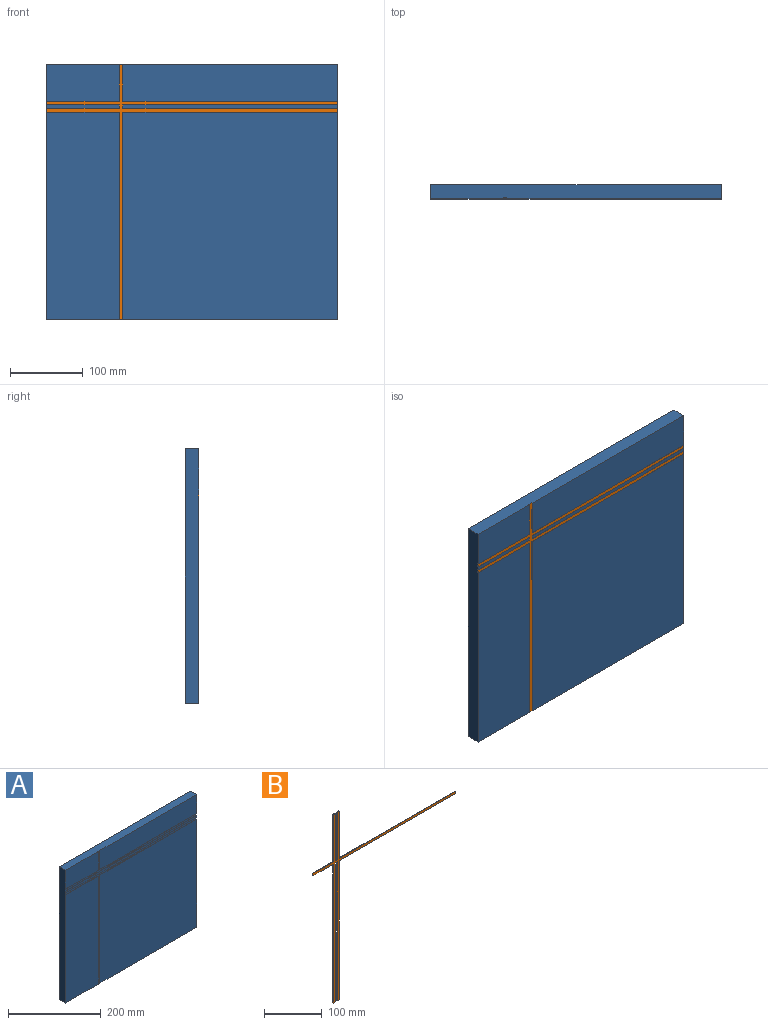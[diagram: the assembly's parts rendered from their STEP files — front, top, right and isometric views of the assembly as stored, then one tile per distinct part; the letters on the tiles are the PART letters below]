
ASSEMBLY  parts=2 mates=1
PART A: 26 faces, bbox 400x19x350 mm
  f0: plane 400x19mm, normal (0,0,1), area 7595mm2, adj f1,f3,f6,f7,f10,f17,f18,f25
  f1: plane 350x19mm, normal (1,0,0), area 6640mm2, adj f0,f2,f3,f4,f8,f10,f12,f13
  f2: plane 295x5mm, normal (0,-1,0), area 1475mm2, adj f1,f13,f14,f15
  f3: plane 295x50mm, normal (0,-1,0), area 14750mm2, adj f0,f1,f16,f17
  f4: plane 295x285mm, normal (0,-1,0), area 84075mm2, adj f1,f8,f11,f12
  f5: plane 100x5mm, normal (0,-1,0), area 500mm2, adj f7,f20,f21,f22
  f6: plane 100x50mm, normal (0,-1,0), area 5000mm2, adj f0,f7,f18,f19
  f7: plane 350x19mm, normal (-1,0,0), area 6640mm2, adj f0,f5,f6,f8,f9,f10,f19,f20
  f8: plane 400x19mm, normal (0,0,-1), area 7595mm2, adj f1,f4,f7,f9,f10,f11,f24,f25
  f9: plane 285x100mm, normal (0,-1,0), area 28500mm2, adj f7,f8,f23,f24
  f10: plane 400x350mm, normal (0,1,0), area 140000mm2, adj f0,f1,f7,f8
  f11: plane 285x1mm, normal (-1,0,0), area 285mm2, adj f4,f8,f12,f25
  f12: plane 295x1mm, normal (0,0,1), area 295mm2, adj f1,f4,f11,f25
  f13: plane 295x1mm, normal (0,0,-1), area 295mm2, adj f1,f2,f14,f25
  f14: plane 5x1mm, normal (-1,0,0), area 5mm2, adj f2,f13,f15,f25
  f15: plane 295x1mm, normal (0,0,1), area 295mm2, adj f1,f2,f14,f25
  f16: plane 295x1mm, normal (0,0,-1), area 295mm2, adj f1,f3,f17,f25
  f17: plane 50x1mm, normal (-1,0,0), area 50mm2, adj f0,f3,f16,f25
  f18: plane 50x1mm, normal (1,0,0), area 50mm2, adj f0,f6,f19,f25
  f19: plane 100x1mm, normal (0,0,-1), area 100mm2, adj f6,f7,f18,f25
  f20: plane 100x1mm, normal (0,0,1), area 100mm2, adj f5,f7,f21,f25
  f21: plane 5x1mm, normal (1,0,0), area 5mm2, adj f5,f20,f22,f25
  f22: plane 100x1mm, normal (0,0,-1), area 100mm2, adj f5,f7,f21,f25
  f23: plane 100x1mm, normal (0,0,1), area 100mm2, adj f7,f9,f24,f25
  f24: plane 285x1mm, normal (1,0,0), area 285mm2, adj f8,f9,f23,f25
  f25: plane 400x350mm, normal (0,-1,0), area 5700mm2, adj f0,f1,f7,f8,f11,f12,f13,f14
PART B: 22 faces, bbox 350x1x400 mm
  f0: plane 100x1mm, normal (1,0,0), area 100mm2, adj f1,f19,f20,f21
  f1: plane 5x1mm, normal (0,0,1), area 5mm2, adj f0,f2,f20,f21
  f2: plane 100x1mm, normal (-1,0,0), area 100mm2, adj f1,f3,f20,f21
  f3: plane 50x1mm, normal (0,0,1), area 50mm2, adj f2,f4,f20,f21
  f4: plane 5x1mm, normal (-1,0,0), area 5mm2, adj f3,f5,f20,f21
  f5: plane 50x1mm, normal (0,0,-1), area 50mm2, adj f4,f6,f20,f21
  f6: plane 295x1mm, normal (-1,0,0), area 295mm2, adj f5,f7,f20,f21
  f7: plane 5x1mm, normal (0,0,-1), area 5mm2, adj f6,f8,f20,f21
  f8: plane 295x1mm, normal (1,0,0), area 295mm2, adj f7,f9,f20,f21
  f9: plane 5x1mm, normal (0,0,-1), area 5mm2, adj f8,f10,f20,f21
  f10: plane 295x1mm, normal (-1,0,0), area 295mm2, adj f9,f11,f20,f21
  f11: plane 5x1mm, normal (0,0,-1), area 5mm2, adj f10,f12,f20,f21
  f12: plane 295x1mm, normal (1,0,0), area 295mm2, adj f11,f13,f20,f21
  f13: plane 285x1mm, normal (0,0,-1), area 285mm2, adj f12,f14,f20,f21
  f14: plane 5x1mm, normal (1,0,0), area 5mm2, adj f13,f15,f20,f21
  f15: plane 285x1mm, normal (0,0,1), area 285mm2, adj f14,f16,f20,f21
  f16: plane 100x1mm, normal (1,0,0), area 100mm2, adj f15,f17,f20,f21
  f17: plane 5x1mm, normal (0,0,1), area 5mm2, adj f16,f18,f20,f21
  f18: plane 100x1mm, normal (-1,0,0), area 100mm2, adj f17,f19,f20,f21
  f19: plane 5x1mm, normal (0,0,1), area 5mm2, adj f0,f18,f20,f21
  f20: plane 400x350mm, normal (0,-1,0), area 5700mm2, adj f0,f1,f2,f3,f4,f5,f6,f7
  f21: plane 400x350mm, normal (0,1,0), area 5700mm2, adj f0,f1,f2,f3,f4,f5,f6,f7
PLACE A t=(-92.25,-13.85,-215.74)mm
PLACE B rot(axis=(0.71,0,-0.71),180deg) t=(75.97,-32.85,-305.24)mm
MATE fastened B.f20 <-> A.f25  axis (0,1,0) through (-168.02,-31.85,-122.32)mm
